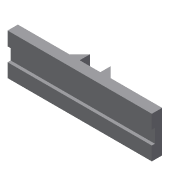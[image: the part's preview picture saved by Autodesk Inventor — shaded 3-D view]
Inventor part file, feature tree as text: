
AUTODESK INVENTOR PART (.ipt)
format: ipt  version: 2015 (Build 190159000, 159)  size: 102,912 bytes
history: native  units: mm
features: sketch x4, extrude x3, split x1
ambient origin geometry x8: Origin, YZ Plane, XZ Plane, XY Plane, X Axis, Y Axis, Z Axis, Center Point
bodies: Solid1 (feature_tree)
feature tree (8):
  extrude  "Extrusion1"  Depth=1.0mm
  extrude  "Extrusion2"  Depth=1.0mm
  extrude  "Extrusion3"  Depth=4.0mm TaperAngle=0.0deg
  split  "Split1"
  sketch  "Sketch1"  dims[d1=7.0mm d2=1.0mm]
  sketch  "Sketch2"  dims[d7=2.0mm d8=1.0mm]
  sketch  "Sketch3"  dims[d9=2.0mm d10=4.0mm d11=0.0mm]
  sketch  "Sketch4"  dims[d14=0.5mm d15=0.5mm d16=2.0mm d17=0.0mm d19=0.5mm d20=2.0mm d21=0.0mm d22=1.3333mm d23=1.3333mm d24=0.3mm]
